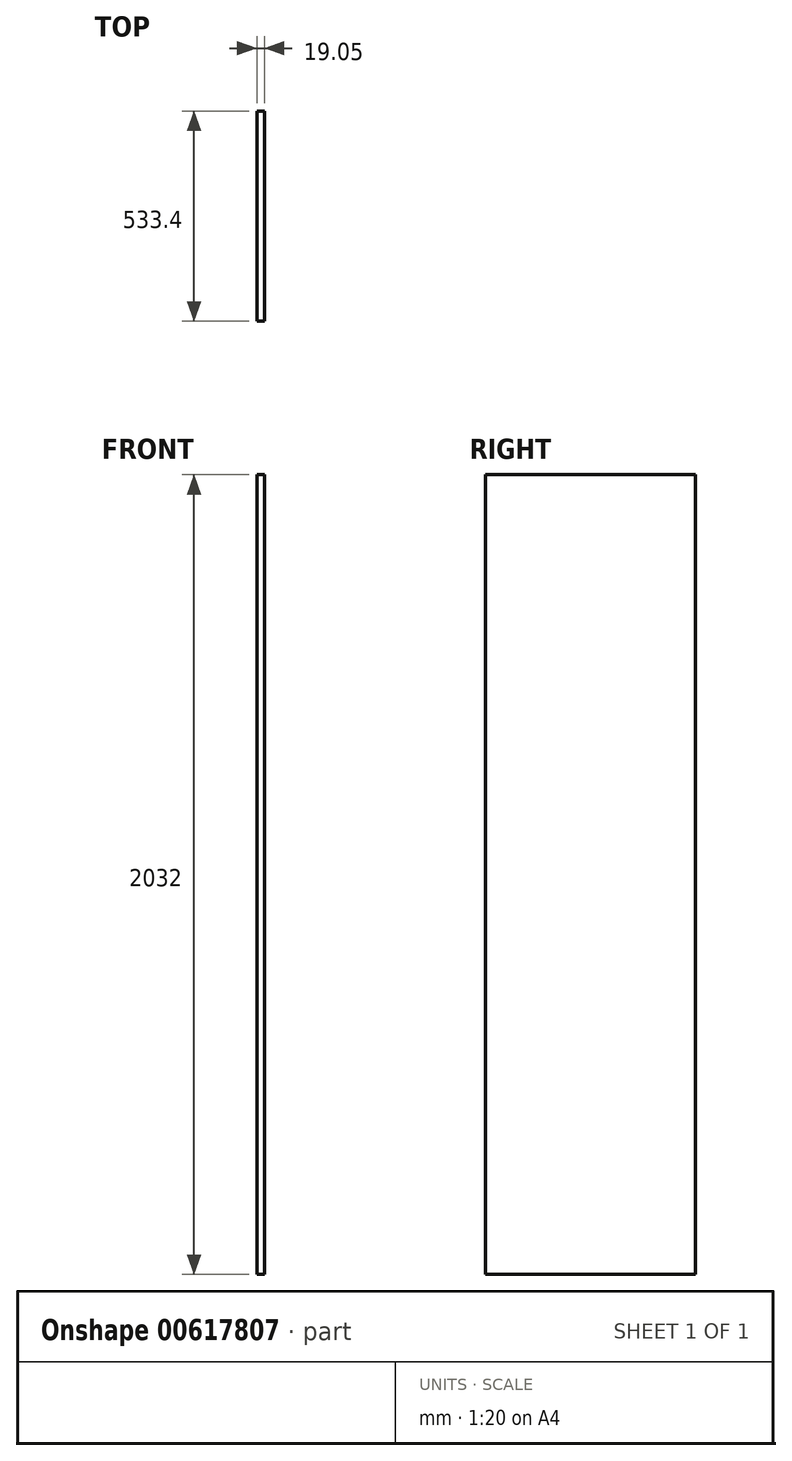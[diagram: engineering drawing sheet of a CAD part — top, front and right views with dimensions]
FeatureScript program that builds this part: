
annotation { "Feature Type Name" : "Feature", "Feature Type Description" : "" }
export const myFeature = defineFeature(function(context is Context, id is Id, definition is map)
    precondition{}
    {
        {
            var Q0;
            Q0=qCreatedBy(makeId("Right.planeOp"),FACE);
            var sketch = newSketch(context, id + "F0", { "sketchPlane" : qUnion([Q0])});
            skLineSegment(sketch, "E0.bottom", {"start": v(266.7, 1016) * mm, "end": v(-266.7, 1016) * mm});
            skLineSegment(sketch, "E0.top", {"start": v(266.7, -1016) * mm, "end": v(-266.7, -1016) * mm});
            skLineSegment(sketch, "E0.left", {"start": v(266.7, 1016) * mm, "end": v(266.7, -1016) * mm});
            skLineSegment(sketch, "E0.right", {"start": v(-266.7, 1016) * mm, "end": v(-266.7, -1016) * mm});
            skPoint(sketch, "E0.middle", {"position": v(0, 0) * mm});
            skSolve(sketch);
        }
        {
            var Q0;
            Q0=makeQuery(id+"F0.imprint","IMPRINT",FACE,{"disambiguationData":[TD([[makeQuery(id+"F0.imprint","IMPRINT",EDGE,{"derivedFrom":sQuery(id+"F0.wireOp",EDGE,"E0.bottom")}),1.0]])]});
            extrude(context, id + "F1", {"entities" : qUnion([Q0]), "depth" : 19.05 * mm, "offsetDistance" : 25.4 * mm});
        }
    });
